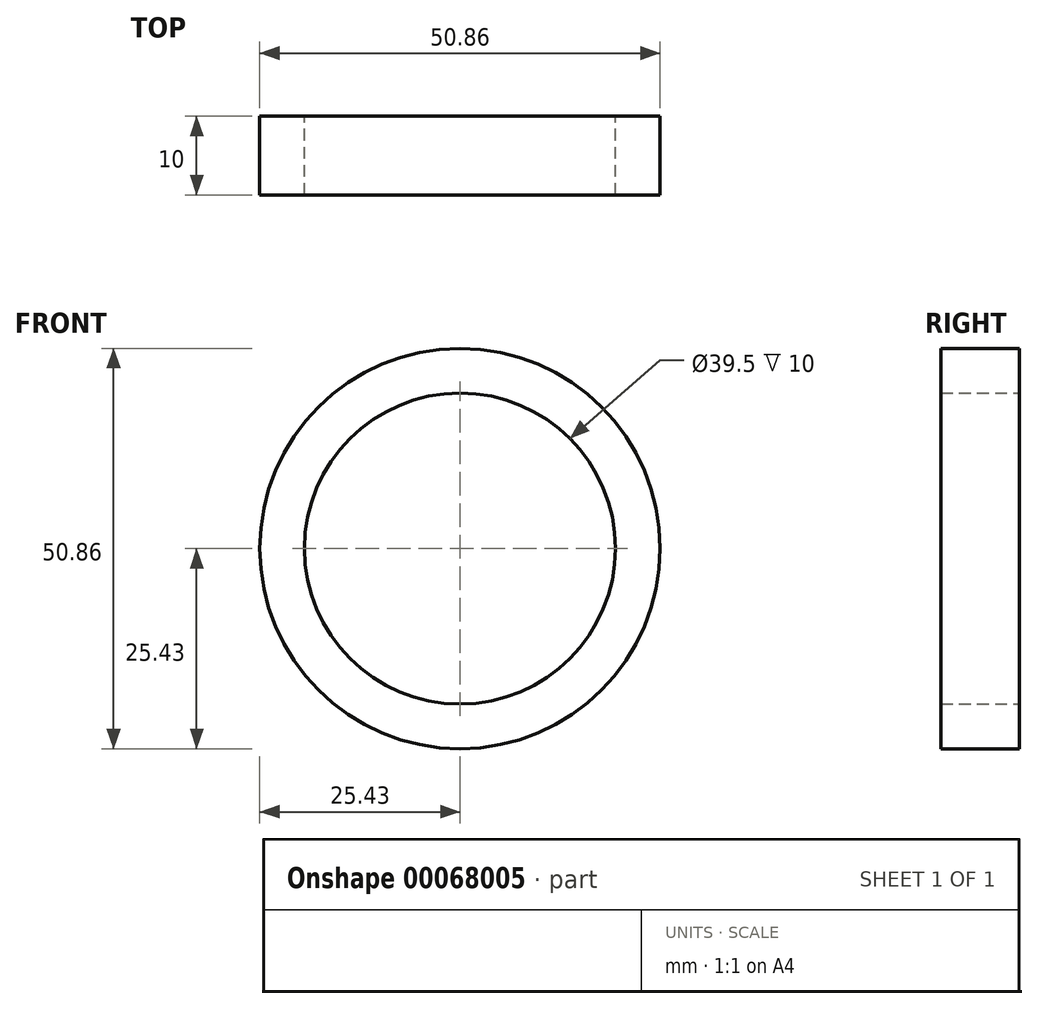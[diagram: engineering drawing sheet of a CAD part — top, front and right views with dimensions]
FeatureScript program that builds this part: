
annotation { "Feature Type Name" : "Feature", "Feature Type Description" : "" }
export const myFeature = defineFeature(function(context is Context, id is Id, definition is map)
    precondition{}
    {
        {
            var Q0;
            Q0=qCreatedBy(makeId("Front.planeOp"),FACE);
            var sketch = newSketch(context, id + "F0", { "sketchPlane" : qUnion([Q0])});
            skCircle(sketch, "E0", {"center": v(0, 0) * mm, "radius": 25.43 * mm});
            skCircle(sketch, "E1", {"center": v(0, 0) * mm, "radius": 15.81 * mm});
            skCircle(sketch, "E2", {"center": v(0, 0) * mm, "radius": 19.75 * mm});
            skSolve(sketch);
        }
        {
            var Q0;
            Q0 = qSketchRegion(id + "F0", true);
            extrude(context, id + "F1", {"entities" : qUnion([Q0]), "depth" : 10 * mm});
        }
    });
